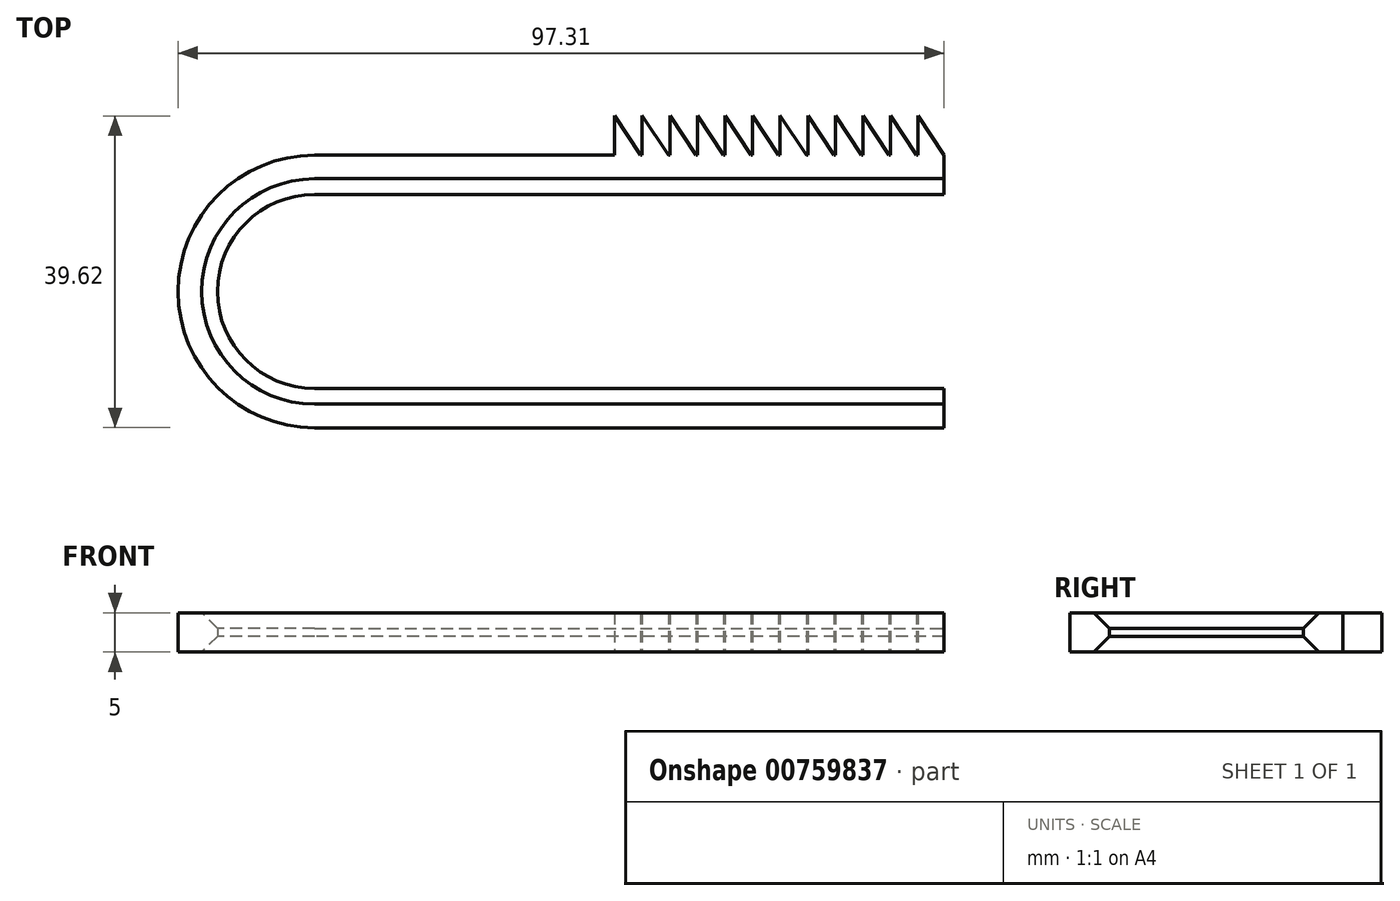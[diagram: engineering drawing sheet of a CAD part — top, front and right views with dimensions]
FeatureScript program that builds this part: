
annotation { "Feature Type Name" : "Feature", "Feature Type Description" : "" }
export const myFeature = defineFeature(function(context is Context, id is Id, definition is map)
    precondition{}
    {
        {
            var Q0;
            Q0=qCreatedBy(makeId("Top.planeOp"),FACE);
            var sketch = newSketch(context, id + "F0", { "sketchPlane" : qUnion([Q0])});
            skArc(sketch, "E0", {"start": v(-64.1, 12.31) * mm, "mid": v(-76.41, 0) * mm, "end": v(-64.1, -12.31) * mm});
            skArc(sketch, "E1", {"start": v(-64.1, 17.31) * mm, "mid": v(-81.41, 0) * mm, "end": v(-64.1, -17.31) * mm});
            skLineSegment(sketch, "E2", {"start": v(-64.1, 17.31) * mm, "end": v(0, 17.31) * mm});
            skLineSegment(sketch, "E3", {"start": v(0, 12.31) * mm, "end": v(-64.1, 12.31) * mm});
            skLineSegment(sketch, "E4", {"start": v(-64.1, -12.31) * mm, "end": v(0, -12.31) * mm});
            skLineSegment(sketch, "E5", {"start": v(0, -17.31) * mm, "end": v(-64.1, -17.31) * mm});
            skLineSegment(sketch, "E6", {"start": v(0, 17.31) * mm, "end": v(15.9, 17.31) * mm});
            skLineSegment(sketch, "E7", {"start": v(0, 12.31) * mm, "end": v(15.9, 12.31) * mm});
            skLineSegment(sketch, "E8", {"start": v(15.9, 12.31) * mm, "end": v(15.9, 17.31) * mm});
            skLineSegment(sketch, "E9", {"start": v(0, -12.31) * mm, "end": v(15.9, -12.31) * mm});
            skLineSegment(sketch, "E10", {"start": v(15.9, -12.31) * mm, "end": v(15.9, -17.31) * mm});
            skLineSegment(sketch, "E11", {"start": v(15.9, -17.31) * mm, "end": v(0, -17.31) * mm});
            skLineSegment(sketch, "E12", {"start": v(15.9, 17.31) * mm, "end": v(12.6, 22.31) * mm});
            skLineSegment(sketch, "E13", {"start": v(12.6, 22.31) * mm, "end": v(12.6, 17.31) * mm});
            skLineSegment(sketch, "E14", {"start": v(12.4, 17.31) * mm, "end": v(9.09, 22.31) * mm});
            skLineSegment(sketch, "E15", {"start": v(9.09, 22.31) * mm, "end": v(9.09, 17.31) * mm});
            skLineSegment(sketch, "E16", {"start": v(8.9, 17.31) * mm, "end": v(5.58, 22.31) * mm});
            skLineSegment(sketch, "E17", {"start": v(5.58, 22.31) * mm, "end": v(5.58, 17.31) * mm});
            skLineSegment(sketch, "E18", {"start": v(5.39, 17.31) * mm, "end": v(2.08, 22.31) * mm});
            skLineSegment(sketch, "E19", {"start": v(2.08, 22.31) * mm, "end": v(2.08, 17.31) * mm});
            skLineSegment(sketch, "E20", {"start": v(1.88, 17.31) * mm, "end": v(-1.43, 22.31) * mm});
            skLineSegment(sketch, "E21", {"start": v(-1.43, 22.31) * mm, "end": v(-1.43, 17.31) * mm});
            skLineSegment(sketch, "E22", {"start": v(-1.62, 17.31) * mm, "end": v(-4.93, 22.31) * mm});
            skLineSegment(sketch, "E23", {"start": v(-4.93, 22.31) * mm, "end": v(-4.93, 17.31) * mm});
            skLineSegment(sketch, "E24", {"start": v(-5.13, 17.31) * mm, "end": v(-8.44, 22.31) * mm});
            skLineSegment(sketch, "E25", {"start": v(-8.44, 22.31) * mm, "end": v(-8.44, 17.31) * mm});
            skLineSegment(sketch, "E26", {"start": v(-8.63, 17.31) * mm, "end": v(-11.94, 22.31) * mm});
            skLineSegment(sketch, "E27", {"start": v(-11.94, 22.31) * mm, "end": v(-11.94, 17.31) * mm});
            skLineSegment(sketch, "E28", {"start": v(-12.14, 17.31) * mm, "end": v(-15.45, 22.31) * mm});
            skLineSegment(sketch, "E29", {"start": v(-15.45, 22.31) * mm, "end": v(-15.45, 17.31) * mm});
            skLineSegment(sketch, "E30", {"start": v(-15.64, 17.31) * mm, "end": v(-18.95, 22.31) * mm});
            skLineSegment(sketch, "E31", {"start": v(-18.95, 22.31) * mm, "end": v(-18.95, 17.31) * mm});
            skLineSegment(sketch, "E32", {"start": v(-19.15, 17.31) * mm, "end": v(-22.46, 22.31) * mm});
            skLineSegment(sketch, "E33", {"start": v(-22.46, 22.31) * mm, "end": v(-22.46, 17.31) * mm});
            skLineSegment(sketch, "E34", {"start": v(-22.65, 17.31) * mm, "end": v(-25.96, 22.31) * mm});
            skLineSegment(sketch, "E35", {"start": v(-25.96, 22.31) * mm, "end": v(-25.96, 17.31) * mm});
            skSolve(sketch);
        }
        {
            var Q0;
            Q0=makeQuery(id+"F0.imprint","IMPRINT",FACE,{"disambiguationData":[TD([[makeQuery(id+"F0.imprint","IMPRINT",EDGE,{"derivedFrom":sQuery(id+"F0.wireOp",EDGE,"E0")}),-1.0]])]});
            var Q1;
            {var subQ0=sQuery(id+"F0.wireOp",EDGE,"658b14cd-3648-4bd3-85a0-d31554900a4c");Q1=makeQuery(id+"F0.imprint","IMPRINT",FACE,{"disambiguationData":[TD([[makeQuery(id+"F0.imprint","IMPRINT",EDGE,{"derivedFrom":subQ0}),1.0]])]});}
            var Q2;
            {var subQ0=sQuery(id+"F0.wireOp",EDGE,"ef1300b1-6ea0-4cbc-b9f5-9cb956dd0833");Q2=makeQuery(id+"F0.imprint","IMPRINT",FACE,{"disambiguationData":[TD([[makeQuery(id+"F0.imprint","IMPRINT",EDGE,{"derivedFrom":subQ0}),1.0]])]});}
            var Q3;
            {var subQ0=sQuery(id+"F0.wireOp",EDGE,"dc3e67c0-503e-4fec-b389-9a7eb3a5a76f");Q3=makeQuery(id+"F0.imprint","IMPRINT",FACE,{"disambiguationData":[TD([[makeQuery(id+"F0.imprint","IMPRINT",EDGE,{"derivedFrom":subQ0}),1.0]])]});}
            var Q4;
            {var subQ0=sQuery(id+"F0.wireOp",EDGE,"4af7fbd2-eee5-43a6-b806-b26ad93c4c9d");Q4=makeQuery(id+"F0.imprint","IMPRINT",FACE,{"disambiguationData":[TD([[makeQuery(id+"F0.imprint","IMPRINT",EDGE,{"derivedFrom":subQ0}),1.0]])]});}
            var Q5;
            {var subQ0=sQuery(id+"F0.wireOp",EDGE,"uHSzluuW-MQIy-aKVM-t9Tw-7AQRKILes7ZT");Q5=makeQuery(id+"F0.imprint","IMPRINT",FACE,{"disambiguationData":[TD([[makeQuery(id+"F0.imprint","IMPRINT",EDGE,{"derivedFrom":subQ0}),1.0]])]});}
            var Q6;
            {var subQ0=sQuery(id+"F0.wireOp",EDGE,"1d141ab8-7c0d-4287-803c-991a334c822d");Q6=makeQuery(id+"F0.imprint","IMPRINT",FACE,{"disambiguationData":[TD([[makeQuery(id+"F0.imprint","IMPRINT",EDGE,{"derivedFrom":subQ0}),1.0]])]});}
            var Q7;
            {var subQ0=sQuery(id+"F0.wireOp",EDGE,"2d38a056-d2e4-441a-b6be-e8787b58152c");Q7=makeQuery(id+"F0.imprint","IMPRINT",FACE,{"disambiguationData":[TD([[makeQuery(id+"F0.imprint","IMPRINT",EDGE,{"derivedFrom":subQ0}),1.0]])]});}
            var Q8;
            {var subQ0=sQuery(id+"F0.wireOp",EDGE,"1a0469bb-50ae-459d-b185-404e74e9096c");Q8=makeQuery(id+"F0.imprint","IMPRINT",FACE,{"disambiguationData":[TD([[makeQuery(id+"F0.imprint","IMPRINT",EDGE,{"derivedFrom":subQ0}),1.0]])]});}
            var Q9;
            {var subQ0=sQuery(id+"F0.wireOp",EDGE,"b6d3f491-8256-4632-8b96-28abfad9a76a");Q9=makeQuery(id+"F0.imprint","IMPRINT",FACE,{"disambiguationData":[TD([[makeQuery(id+"F0.imprint","IMPRINT",EDGE,{"derivedFrom":subQ0}),1.0]])]});}
            var Q10;
            {var subQ0=sQuery(id+"F0.wireOp",EDGE,"73418f5e-84c6-4f0d-a42e-ffde0efb4e01");Q10=makeQuery(id+"F0.imprint","IMPRINT",FACE,{"disambiguationData":[TD([[makeQuery(id+"F0.imprint","IMPRINT",EDGE,{"derivedFrom":subQ0}),1.0]])]});}
            var Q11;
            {var subQ0=sQuery(id+"F0.wireOp",EDGE,"2e094786-b8f4-49e1-be37-78e41d7a75c1");Q11=makeQuery(id+"F0.imprint","IMPRINT",FACE,{"disambiguationData":[TD([[makeQuery(id+"F0.imprint","IMPRINT",EDGE,{"derivedFrom":subQ0}),1.0]])]});}
            var Q12;
            {var subQ0=sQuery(id+"F0.wireOp",EDGE,"a73edc00-3d9b-41d8-ab40-c2ee9d129ba2");Q12=makeQuery(id+"F0.imprint","IMPRINT",FACE,{"disambiguationData":[TD([[makeQuery(id+"F0.imprint","IMPRINT",EDGE,{"derivedFrom":subQ0}),1.0]])]});}
            var Q13;
            {var subQ0=sQuery(id+"F0.wireOp",EDGE,"728d27a6-e658-49e7-ac88-73856cb4e8fa");Q13=makeQuery(id+"F0.imprint","IMPRINT",FACE,{"disambiguationData":[TD([[makeQuery(id+"F0.imprint","IMPRINT",EDGE,{"derivedFrom":subQ0}),1.0]])]});}
            var Q14;
            {var subQ0=sQuery(id+"F0.wireOp",EDGE,"edde2817-3310-49ca-a794-cd1fce4e8bd9");Q14=makeQuery(id+"F0.imprint","IMPRINT",FACE,{"disambiguationData":[TD([[makeQuery(id+"F0.imprint","IMPRINT",EDGE,{"derivedFrom":subQ0}),1.0]])]});}
            var Q15;
            {var subQ0=sQuery(id+"F0.wireOp",EDGE,"d2fb218f-61cb-4b6d-b45a-44ce93ea4c27");Q15=makeQuery(id+"F0.imprint","IMPRINT",FACE,{"disambiguationData":[TD([[makeQuery(id+"F0.imprint","IMPRINT",EDGE,{"derivedFrom":subQ0}),1.0]])]});}
            var Q16;
            {var subQ0=sQuery(id+"F0.wireOp",EDGE,"cc7bd8e1-74bc-4a19-b812-b8352a18db9d");Q16=makeQuery(id+"F0.imprint","IMPRINT",FACE,{"disambiguationData":[TD([[makeQuery(id+"F0.imprint","IMPRINT",EDGE,{"derivedFrom":subQ0}),1.0]])]});}
            var Q17;
            {var subQ0=sQuery(id+"F0.wireOp",EDGE,"a76a726a-3fd8-4023-a4b6-8f2075fb759a");Q17=makeQuery(id+"F0.imprint","IMPRINT",FACE,{"disambiguationData":[TD([[makeQuery(id+"F0.imprint","IMPRINT",EDGE,{"derivedFrom":subQ0}),1.0]])]});}
            var Q18;
            {var subQ0=sQuery(id+"F0.wireOp",EDGE,"8a4f437d-85eb-45d3-b33b-8c570e5dabbb");Q18=makeQuery(id+"F0.imprint","IMPRINT",FACE,{"disambiguationData":[TD([[makeQuery(id+"F0.imprint","IMPRINT",EDGE,{"derivedFrom":subQ0}),1.0]])]});}
            var Q19;
            {var subQ0=sQuery(id+"F0.wireOp",EDGE,"E12");Q19=makeQuery(id+"F0.imprint","IMPRINT",FACE,{"disambiguationData":[TD([[makeQuery(id+"F0.imprint","IMPRINT",EDGE,{"derivedFrom":subQ0}),1.0]])]});}
            var Q20;
            {var subQ0=sQuery(id+"F0.wireOp",EDGE,"E14");Q20=makeQuery(id+"F0.imprint","IMPRINT",FACE,{"disambiguationData":[TD([[makeQuery(id+"F0.imprint","IMPRINT",EDGE,{"derivedFrom":subQ0}),1.0]])]});}
            var Q21;
            {var subQ0=sQuery(id+"F0.wireOp",EDGE,"E16");Q21=makeQuery(id+"F0.imprint","IMPRINT",FACE,{"disambiguationData":[TD([[makeQuery(id+"F0.imprint","IMPRINT",EDGE,{"derivedFrom":subQ0}),1.0]])]});}
            var Q22;
            {var subQ0=sQuery(id+"F0.wireOp",EDGE,"E18");Q22=makeQuery(id+"F0.imprint","IMPRINT",FACE,{"disambiguationData":[TD([[makeQuery(id+"F0.imprint","IMPRINT",EDGE,{"derivedFrom":subQ0}),1.0]])]});}
            var Q23;
            {var subQ4=sQuery(id+"F0.wireOp",EDGE,"E20");Q23=makeQuery(id+"F0.imprint","IMPRINT",FACE,{"disambiguationData":[TD([[makeQuery(id+"F0.imprint","IMPRINT",EDGE,{"derivedFrom":subQ4}),1.0]])]});}
            var Q24;
            {var subQ0=sQuery(id+"F0.wireOp",EDGE,"E22");Q24=makeQuery(id+"F0.imprint","IMPRINT",FACE,{"disambiguationData":[TD([[makeQuery(id+"F0.imprint","IMPRINT",EDGE,{"derivedFrom":subQ0}),1.0]])]});}
            var Q25;
            {var subQ0=sQuery(id+"F0.wireOp",EDGE,"E24");Q25=makeQuery(id+"F0.imprint","IMPRINT",FACE,{"disambiguationData":[TD([[makeQuery(id+"F0.imprint","IMPRINT",EDGE,{"derivedFrom":subQ0}),1.0]])]});}
            var Q26;
            {var subQ0=sQuery(id+"F0.wireOp",EDGE,"E26");Q26=makeQuery(id+"F0.imprint","IMPRINT",FACE,{"disambiguationData":[TD([[makeQuery(id+"F0.imprint","IMPRINT",EDGE,{"derivedFrom":subQ0}),1.0]])]});}
            var Q27;
            {var subQ0=sQuery(id+"F0.wireOp",EDGE,"E28");Q27=makeQuery(id+"F0.imprint","IMPRINT",FACE,{"disambiguationData":[TD([[makeQuery(id+"F0.imprint","IMPRINT",EDGE,{"derivedFrom":subQ0}),1.0]])]});}
            var Q28;
            {var subQ0=sQuery(id+"F0.wireOp",EDGE,"E30");Q28=makeQuery(id+"F0.imprint","IMPRINT",FACE,{"disambiguationData":[TD([[makeQuery(id+"F0.imprint","IMPRINT",EDGE,{"derivedFrom":subQ0}),1.0]])]});}
            var Q29;
            {var subQ0=sQuery(id+"F0.wireOp",EDGE,"E32");Q29=makeQuery(id+"F0.imprint","IMPRINT",FACE,{"disambiguationData":[TD([[makeQuery(id+"F0.imprint","IMPRINT",EDGE,{"derivedFrom":subQ0}),1.0]])]});}
            var Q30;
            {var subQ0=sQuery(id+"F0.wireOp",EDGE,"E34");Q30=makeQuery(id+"F0.imprint","IMPRINT",FACE,{"disambiguationData":[TD([[makeQuery(id+"F0.imprint","IMPRINT",EDGE,{"derivedFrom":subQ0}),1.0]])]});}
            extrude(context, id + "F1", {"entities" : qUnion([Q0, Q1, Q2, Q3, Q4, Q5, Q6, Q7, Q8, Q9, Q10, Q11, Q12, Q13, Q14, Q15, Q16, Q17, Q18, Q19, Q20, Q21, Q22, Q23, Q24, Q25, Q26, Q27, Q28, Q29, Q30]), "depth" : 5 * mm, "offsetDistance" : 25 * mm});
        }
        {
            var Q0;
            Q0=makeQuery(id+"F1.opExtrude","CAP_EDGE",EDGE,{"disambiguationData":[OSD([sQuery(id+"F0.wireOp",EDGE,"E0")])],"isStart":false});
            var Q1;
            Q1=makeQuery(id+"F1.opExtrude","CAP_EDGE",EDGE,{"disambiguationData":[OSD([sQuery(id+"F0.wireOp",EDGE,"E0")])],"isStart":true});
            chamfer(context, id + "F2", {"entities" : qUnion([Q0, Q1]), "width" : 2 * mm, "tangentPropagation" : true});
        }
    });
